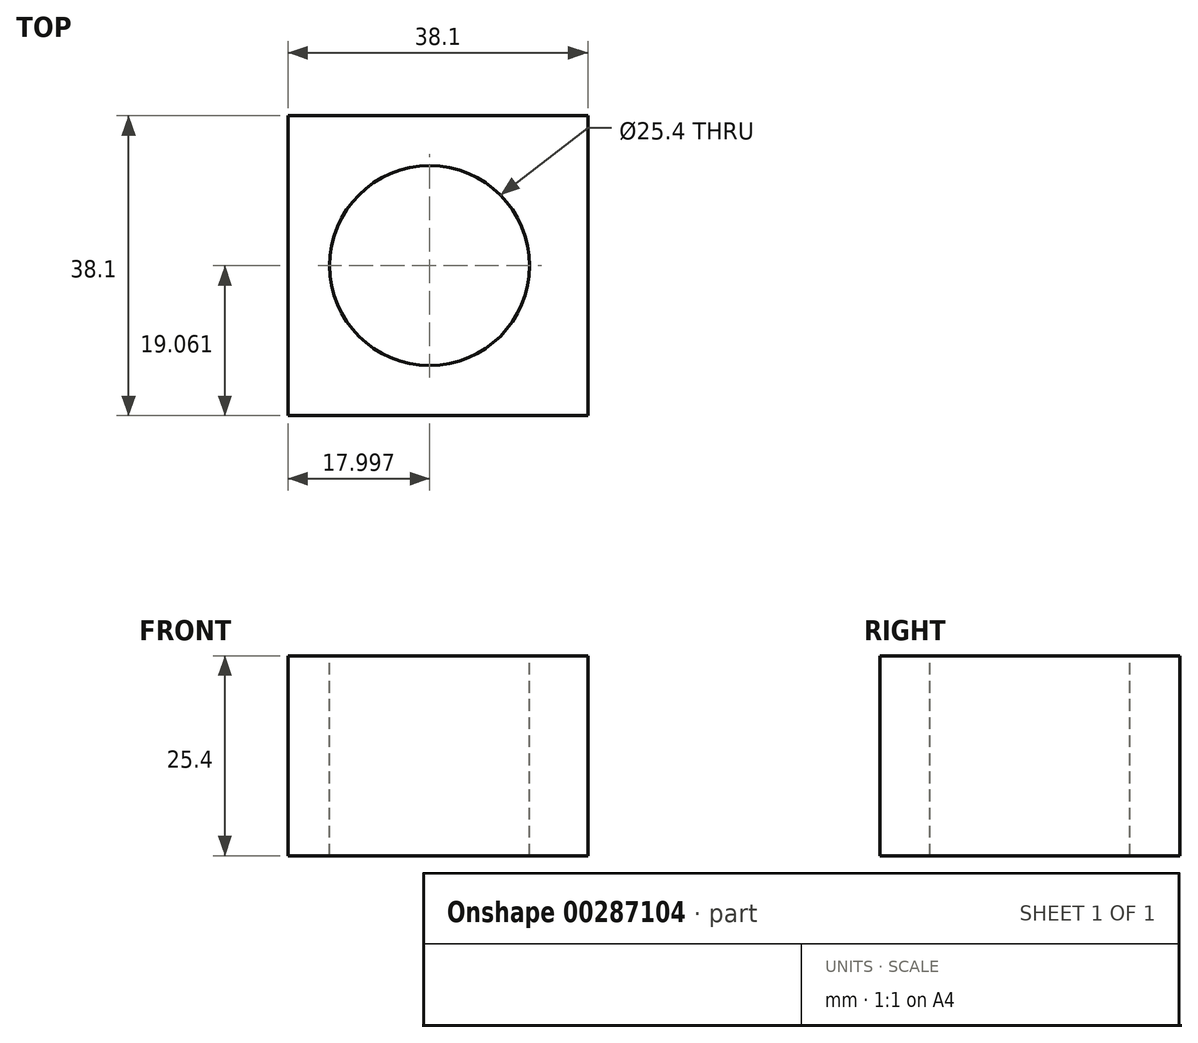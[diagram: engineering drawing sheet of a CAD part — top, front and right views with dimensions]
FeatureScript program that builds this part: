
annotation { "Feature Type Name" : "Feature", "Feature Type Description" : "" }
export const myFeature = defineFeature(function(context is Context, id is Id, definition is map)
    precondition{}
    {
        {
            var Q0;
            Q0=qCreatedBy(makeId("Top.planeOp"),FACE);
            var sketch = newSketch(context, id + "F0", { "sketchPlane" : qUnion([Q0])});
            skLineSegment(sketch, "E0.bottom", {"start": v(0, 0) * mm, "end": v(38.1, 0) * mm});
            skLineSegment(sketch, "E0.top", {"start": v(0, 38.1) * mm, "end": v(38.1, 38.1) * mm});
            skLineSegment(sketch, "E0.left", {"start": v(0, 0) * mm, "end": v(0, 38.1) * mm});
            skLineSegment(sketch, "E0.right", {"start": v(38.1, 0) * mm, "end": v(38.1, 38.1) * mm});
            skSolve(sketch);
        }
        {
            var Q0;
            Q0 = qSketchRegion(id + "F0", true);
            extrude(context, id + "F1", {"entities" : qUnion([Q0]), "depth" : 25.4 * mm});
        }
        {
            var Q0;
            Q0=makeQuery(id+"F1.opExtrude","CAP_FACE",FACE,{"disambiguationData":[OSD([sQuery(id+"F0.wireOp",EDGE,"E0.bottom"),sQuery(id+"F0.wireOp",EDGE,"E0.top"),sQuery(id+"F0.wireOp",EDGE,"E0.left"),sQuery(id+"F0.wireOp",EDGE,"E0.right")])],"isStart":false});
            var sketch = newSketch(context, id + "F2", { "sketchPlane" : qUnion([Q0])});
            skCircle(sketch, "E1", {"center": v(18, 19.06) * mm, "radius": 12.7 * mm});
            skLineSegment(sketch, "E2", {"start": v(18, 19.06) * mm, "end": v(18, 38.1) * mm});
            skLineSegment(sketch, "E3", {"start": v(18, 38.1) * mm, "end": v(18, 19.06) * mm, "construction": true});
            skLineSegment(sketch, "E4", {"start": v(38.1, 19.06) * mm, "end": v(18, 19.06) * mm, "construction": true});
            skSolve(sketch);
        }
        {
            var Q0;
            Q0 = qSketchRegion(id + "F2", true);
            extrude(context, id + "F3", {"entities" : qUnion([Q0]), "operationType" : NewBodyOperationType.REMOVE, "endBound" : BoundingType.THROUGH_ALL, "oppositeDirection" : true, "depth" : 25.4 * mm});
        }
    });
